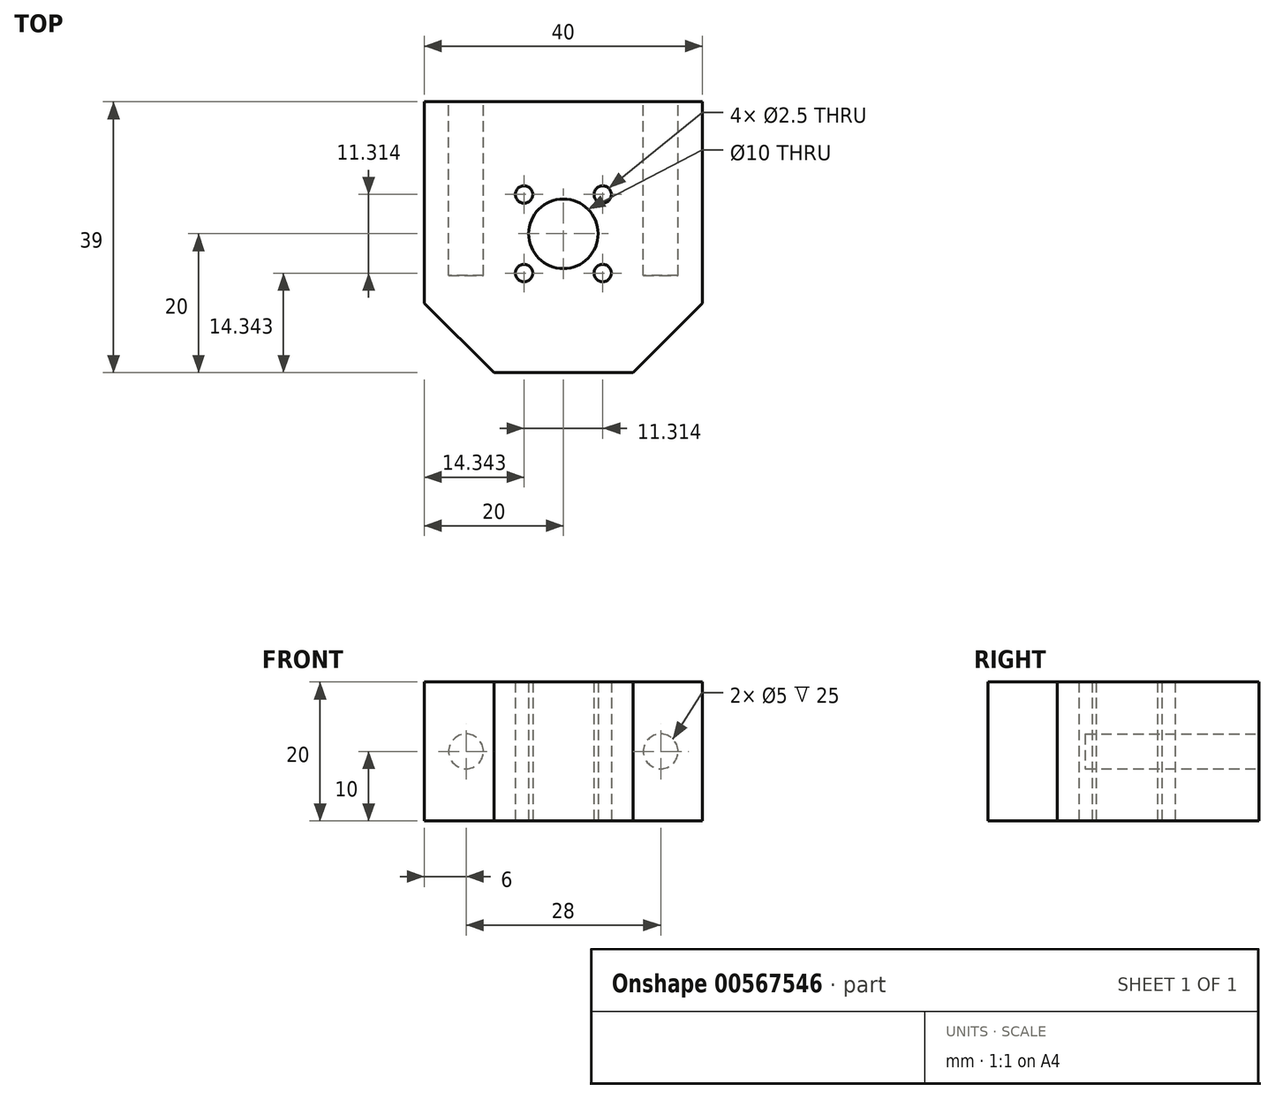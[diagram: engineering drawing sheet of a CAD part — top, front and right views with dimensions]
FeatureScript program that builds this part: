
annotation { "Feature Type Name" : "Feature", "Feature Type Description" : "" }
export const myFeature = defineFeature(function(context is Context, id is Id, definition is map)
    precondition{}
    {
        {
            var Q0;
            Q0=qCreatedBy(makeId("Top.planeOp"),FACE);
            var sketch = newSketch(context, id + "F0", { "sketchPlane" : qUnion([Q0])});
            skLineSegment(sketch, "E0.bottom", {"start": v(20, -19.5) * mm, "end": v(-20, -19.5) * mm});
            skLineSegment(sketch, "E0.top", {"start": v(20, 19.5) * mm, "end": v(-20, 19.5) * mm});
            skLineSegment(sketch, "E0.left", {"start": v(20, -19.5) * mm, "end": v(20, 19.5) * mm});
            skLineSegment(sketch, "E0.right", {"start": v(-20, -19.5) * mm, "end": v(-20, 19.5) * mm});
            skPoint(sketch, "E0.middle", {"position": v(0, 0) * mm});
            skCircle(sketch, "E1", {"center": v(0, 0.5) * mm, "radius": 5 * mm});
            skCircle(sketch, "E2", {"center": v(0, 0.5) * mm, "radius": 8 * mm, "construction": true});
            skCircle(sketch, "E3", {"center": v(0, 0.5) * mm, "radius": 15 * mm, "construction": true});
            skLineSegment(sketch, "E4.bottom", {"start": v(5.66, -5.16) * mm, "end": v(-5.66, -5.16) * mm, "construction": true});
            skLineSegment(sketch, "E4.top", {"start": v(5.66, 6.16) * mm, "end": v(-5.66, 6.16) * mm, "construction": true});
            skLineSegment(sketch, "E4.left", {"start": v(5.66, -5.16) * mm, "end": v(5.66, 6.16) * mm, "construction": true});
            skLineSegment(sketch, "E4.right", {"start": v(-5.66, -5.16) * mm, "end": v(-5.66, 6.16) * mm, "construction": true});
            skCircle(sketch, "E5", {"center": v(-5.66, 6.16) * mm, "radius": 1.25 * mm});
            skCircle(sketch, "E6", {"center": v(5.66, 6.16) * mm, "radius": 1.25 * mm});
            skCircle(sketch, "E7", {"center": v(5.66, -5.16) * mm, "radius": 1.25 * mm});
            skCircle(sketch, "E8", {"center": v(-5.66, -5.16) * mm, "radius": 1.25 * mm});
            skSolve(sketch);
        }
        {
            var Q0;
            Q0=makeQuery(id+"F0.imprint","IMPRINT",FACE,{"disambiguationData":[TD([[makeQuery(id+"F0.imprint","IMPRINT",EDGE,{"derivedFrom":sQuery(id+"F0.wireOp",EDGE,"E0.bottom")}),-1.0]])]});
            extrude(context, id + "F1", {"entities" : qUnion([Q0]), "depth" : 20 * mm, "offsetDistance" : 25 * mm});
        }
        {
            var Q0;
            Q0=makeQuery(id+"F1.opExtrude","SWEPT_EDGE",EDGE,{"disambiguationData":[OSD([sQuery(id+"F0.wireOp",EDGE,"E0.bottom"),sQuery(id+"F0.wireOp",EDGE,"E0.right")])]});
            var Q1;
            Q1=makeQuery(id+"F1.opExtrude","SWEPT_EDGE",EDGE,{"disambiguationData":[OSD([sQuery(id+"F0.wireOp",EDGE,"E0.bottom"),sQuery(id+"F0.wireOp",EDGE,"E0.left")])]});
            chamfer(context, id + "F2", {"entities" : qUnion([Q0, Q1]), "width" : 10 * mm, "tangentPropagation" : true});
        }
        {
            var Q0;
            Q0=makeQuery(id+"F1.opExtrude","SWEPT_FACE",FACE,{"disambiguationData":[OSD([sQuery(id+"F0.wireOp",EDGE,"E0.top")])]});
            var sketch = newSketch(context, id + "F3", { "sketchPlane" : qUnion([Q0])});
            skCircle(sketch, "E9", {"center": v(14, 10) * mm, "radius": 2.5 * mm});
            skPoint(sketch, "E9.centerSnap0", {"position": v(20, 10) * mm});
            skCircle(sketch, "E10", {"center": v(-14, 10) * mm, "radius": 2.5 * mm});
            skPoint(sketch, "E10.centerSnap0", {"position": v(-20, 10) * mm});
            skLineSegment(sketch, "E11", {"start": v(-14, 10) * mm, "end": v(-20, 10) * mm, "construction": true});
            skLineSegment(sketch, "E12", {"start": v(14, 10) * mm, "end": v(20, 10) * mm, "construction": true});
            skSolve(sketch);
        }
        {
            var Q0;
            Q0=makeQuery(id+"F3.imprint","IMPRINT",FACE,{"disambiguationData":[TD([[makeQuery(id+"F3.imprint","IMPRINT",EDGE,{"derivedFrom":sQuery(id+"F3.wireOp",EDGE,"E9")}),1.0]])]});
            var Q1;
            Q1=makeQuery(id+"F3.imprint","IMPRINT",FACE,{"disambiguationData":[TD([[makeQuery(id+"F3.imprint","IMPRINT",EDGE,{"derivedFrom":sQuery(id+"F3.wireOp",EDGE,"E10")}),1.0]])]});
            extrude(context, id + "F4", {"entities" : qUnion([Q0, Q1]), "operationType" : NewBodyOperationType.REMOVE, "oppositeDirection" : true, "depth" : 25 * mm, "offsetDistance" : 25 * mm});
        }
    });
